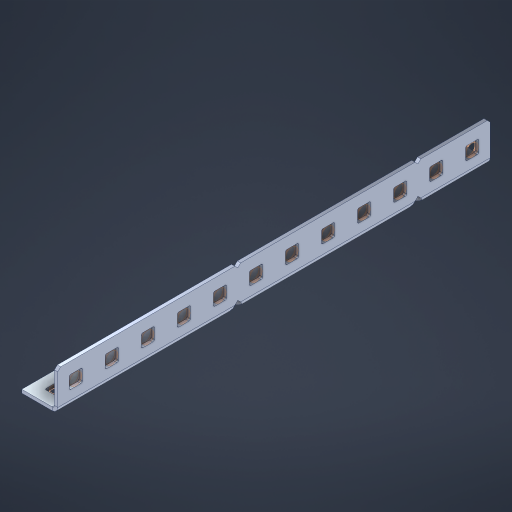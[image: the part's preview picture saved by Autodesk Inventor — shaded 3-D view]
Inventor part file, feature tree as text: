
AUTODESK INVENTOR PART (.ipt)
format: ipt  version: 2023 (Build 270158000, 158)  size: 595,968 bytes
history: native  units: in
note: dims shown in document units (in); Inventor stores cm internally (conversion verified against a paired STEP export)
features: other x29, extrude x23, sheet_metal_op x10, sketch x8, mirror x1, pattern_linear x1, chamfer x1
ambient origin geometry x8: Origin, YZ Plane, XZ Plane, XY Plane, X Axis, Y Axis, Z Axis, Center Point
bodies: Solid1 (feature_tree), Body (feature_tree)
feature tree (73):
  other  "Flange Pattern Plane"
  sheet_metal_op  "Flange Pattern"
  sheet_metal_op  "Body Pattern"
  other  "Arc Length"
  mirror  "Notch Mirror"
  pattern_linear  "Notch Pattern"  Spacing1=0.1875in  [1 undecoded]
  chamfer  "End Chamfer"
  extrude  "Half Cut"  Depth=0.0469in
  sketch  "Sketch1"  dims[d0=2.5in]
  other  "Plate1"
  sketch  "Sketch2"  dims[d1=6.0in]
  other  "Plate2"
  sheet_metal_op  "Bend1"
  sheet_metal_op  "Corner1"
  sketch  "Sketch3"  dims[d2=0.0469in]
  other  "Flange Pattern Sketch"
  sketch  "Sketch7"  dims[d3=0.0469in]
  other  "Srf1"
  other  "Srf2"
  sketch  "Sketch8"  dims[d4=0.0234in]
  sketch  "Sketch9"  dims[d5=0.0938in]
  other  "Srf91"
  sheet_metal_op  "Body Pattern Sketch"
  other  "Srf92"
  sketch  "Sketch13"  dims[d6=0.0469in]
  sketch  "Sketch14"  dims[d7=0.5in d8=90.0deg d9=0.0312in d10=0.1875in d11=0.0469in d12=0.0469in d16=0.182in d17=0.02in d18=0.0469in d19=0.0in d20=0.25in d21=0.25in d46=0.172in d47=1.0in d48=0.0in d49=0.182in d50=0.02in d51=0.25in d52=0.25in d53=0.0469in d54=0.0in d55=0.172in d56=1.0in d57=0.0in d60=4.7244in d62=0.5in d63=0.3937in d65=0.5in d85=0.1227in d86=0.1659in d88=0.04in d89=0.0469in d90=0.0in d91=0.04in d92=0.0491in d95=2.5in d96=0.04in d97=0.25in d98=45.0deg d101=0.0in d102=2.497in d131=0.5in d132=4.7244in d134=0.5in d139=0.5in]
  other  "Srf856"
  other  "Srf1310"
  other  "Srf1311"
  other  "Srf1312"
  other  "Srf1376"
  other  "Srf1377"
  other  "Srf1728"
  other  "Srf1755"
  other  "Srf1878"
  other  "Srf1879"
  other  "Srf1880"
  other  "Srf1881"
  other  "Srf1882"
  other  "Srf1883"
  other  "Srf1942"
  other  "Srf1943"
  other  "Srf1944"
  other  "Srf1945"
  other  "Srf1946"
  other  "Srf1947"
  sheet_metal_op  "Flange Stamp"
  sheet_metal_op  "Flange Circle"
  sheet_metal_op  "Body Stamp"
  sheet_metal_op  "Body Circle"
  sheet_metal_op  "Notch"
  extrude  "ExtrusionSrf2"  Depth=0.0469in
  extrude  "ExtrusionSrf92"  Depth=0.5in
  extrude  "ExtrusionSrf856"  Depth=0.02in
  extrude  "ExtrusionSrf1310"  Depth=0.0469in
  extrude  "ExtrusionSrf1311"  TaperAngle=0.0deg  [1 undecoded]
  extrude  "ExtrusionSrf1312"  Depth=0.5in
  extrude  "ExtrusionSrf1376"  Depth=0.5in
  extrude  "ExtrusionSrf1377"  Depth=0.5in
  extrude  "ExtrusionSrf1728"  Depth=0.5in TaperAngle=0.0deg
  extrude  "ExtrusionSrf1755"  Depth=0.5in
  extrude  "ExtrusionSrf1878"  Depth=0.02in
  extrude  "ExtrusionSrf1879"  Depth=0.5in
  extrude  "ExtrusionSrf1880"  Depth=0.5in
  extrude  "ExtrusionSrf1881"  Depth=0.0469in
  extrude  "ExtrusionSrf1882"  TaperAngle=0.0deg  [1 undecoded]
  extrude  "ExtrusionSrf1883"  Depth=0.5in
  extrude  "ExtrusionSrf1942"  Depth=0.5in TaperAngle=0.0deg
  extrude  "ExtrusionSrf1943"  Depth=0.5in
  extrude  "ExtrusionSrf1944"  Depth=0.5in
  extrude  "ExtrusionSrf1945"  Depth=0.5in
  extrude  "ExtrusionSrf1946"  Depth=0.5in
  extrude  "ExtrusionSrf1947"  Depth=0.5in
note: 3 required parameter values undecoded (feature->parameter linkage not recoverable at this tier; creation-order binding heuristic only, values carry confidence <= 0.55)
